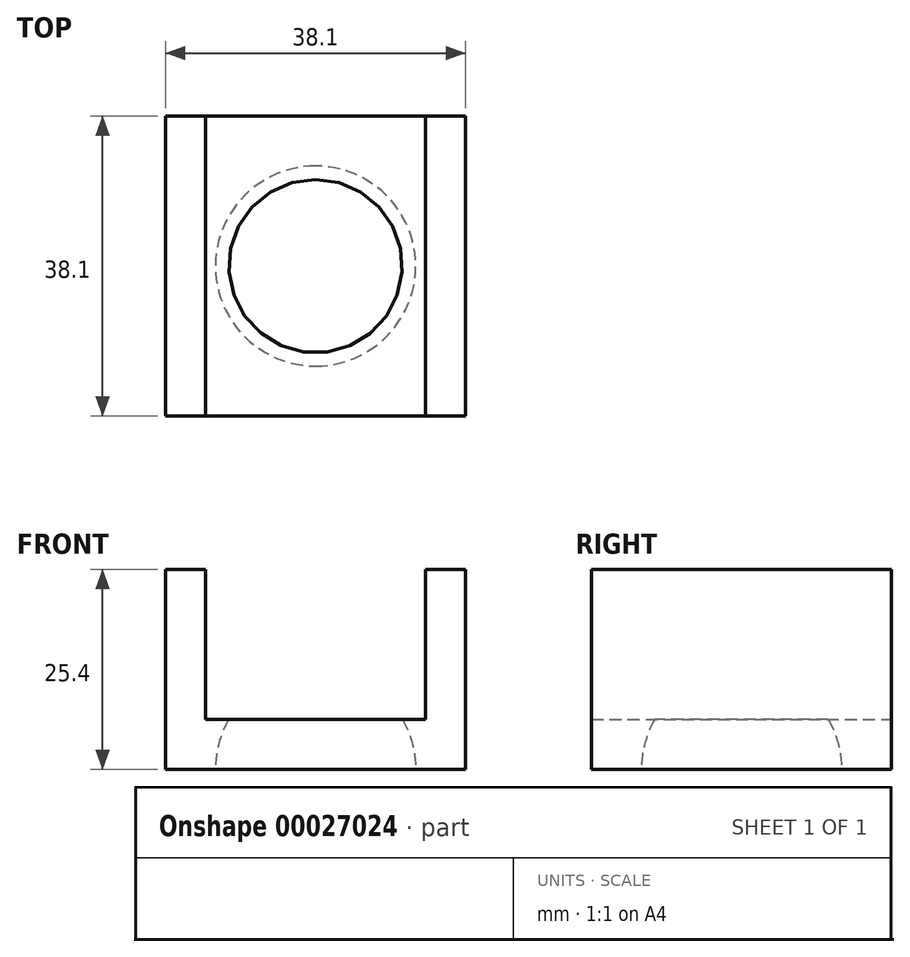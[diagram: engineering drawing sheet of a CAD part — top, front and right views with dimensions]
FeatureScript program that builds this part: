
annotation { "Feature Type Name" : "Feature", "Feature Type Description" : "" }
export const myFeature = defineFeature(function(context is Context, id is Id, definition is map)
    precondition{}
    {
        {
            var Q0;
            Q0=qCreatedBy(makeId("Front.planeOp"),FACE);
            var sketch = newSketch(context, id + "F0", { "sketchPlane" : qUnion([Q0])});
            skLineSegment(sketch, "E0.bottom", {"start": v(-20.99, 16.53) * mm, "end": v(-15.9, 16.53) * mm});
            skLineSegment(sketch, "E0.top", {"start": v(-20.99, -8.87) * mm, "end": v(17.11, -8.87) * mm});
            skLineSegment(sketch, "E0.left", {"start": v(-20.99, 16.53) * mm, "end": v(-20.99, -8.87) * mm});
            skLineSegment(sketch, "E0.right", {"start": v(17.11, 16.53) * mm, "end": v(17.11, -8.87) * mm});
            skLineSegment(sketch, "E1", {"start": v(-15.9, 16.53) * mm, "end": v(-15.9, -2.52) * mm});
            skLineSegment(sketch, "E2", {"start": v(-15.9, -2.52) * mm, "end": v(12.03, -2.52) * mm});
            skLineSegment(sketch, "E3", {"start": v(12.03, -2.52) * mm, "end": v(12.03, 16.53) * mm});
            skLineSegment(sketch, "E4.trimOffspring", {"start": v(12.03, 16.53) * mm, "end": v(17.11, 16.53) * mm});
            skSolve(sketch);
        }
        {
            var Q0;
            Q0=makeQuery(id+"F0.imprint","IMPRINT",FACE,{"disambiguationData":[TD([[makeQuery(id+"F0.imprint","IMPRINT",EDGE,{"derivedFrom":sQuery(id+"F0.wireOp",EDGE,"E0.bottom")}),-1.0]])]});
            extrude(context, id + "F1", {"entities" : qUnion([Q0]), "depth" : 38.1 * mm});
        }
        {
            var Q0;
            Q0=makeQuery(id+"F1.opExtrude","SWEPT_FACE",FACE,{"disambiguationData":[OSD([sQuery(id+"F0.wireOp",EDGE,"E0.top")])]});
            var sketch = newSketch(context, id + "F2", { "sketchPlane" : qUnion([Q0])});
            skPoint(sketch, "E5", {"position": v(-1.94, 19.05) * mm});
            skLineSegment(sketch, "E6", {"start": v(-1.94, 19.05) * mm, "end": v(-1.94, 31.75) * mm});
            skLineSegment(sketch, "E7", {"start": v(-1.94, 19.05) * mm, "end": v(-1.94, 6.35) * mm});
            skArc(sketch, "E8", {"start": v(-1.94, 31.75) * mm, "mid": v(-14.66, 19.05) * mm, "end": v(-1.94, 6.35) * mm});
            skSolve(sketch);
        }
        {
            var Q0;
            Q0=makeQuery(id+"F2.imprint","IMPRINT",FACE,{"disambiguationData":[TD([[makeQuery(id+"F2.imprint","IMPRINT",EDGE,{"derivedFrom":sQuery(id+"F2.wireOp",EDGE,"E6")}),1.0]])]});
            var Q1;
            Q1=sQuery(id+"F2.wireOp",EDGE,"E6");
            revolve(context, id + "F3", {"operationType" : NewBodyOperationType.REMOVE, "entities" : qUnion([Q0]), "axis" : qUnion([Q1]), "revolveType" : RevolveType.FULL, "oppositeDirection" : true});
        }
    });
